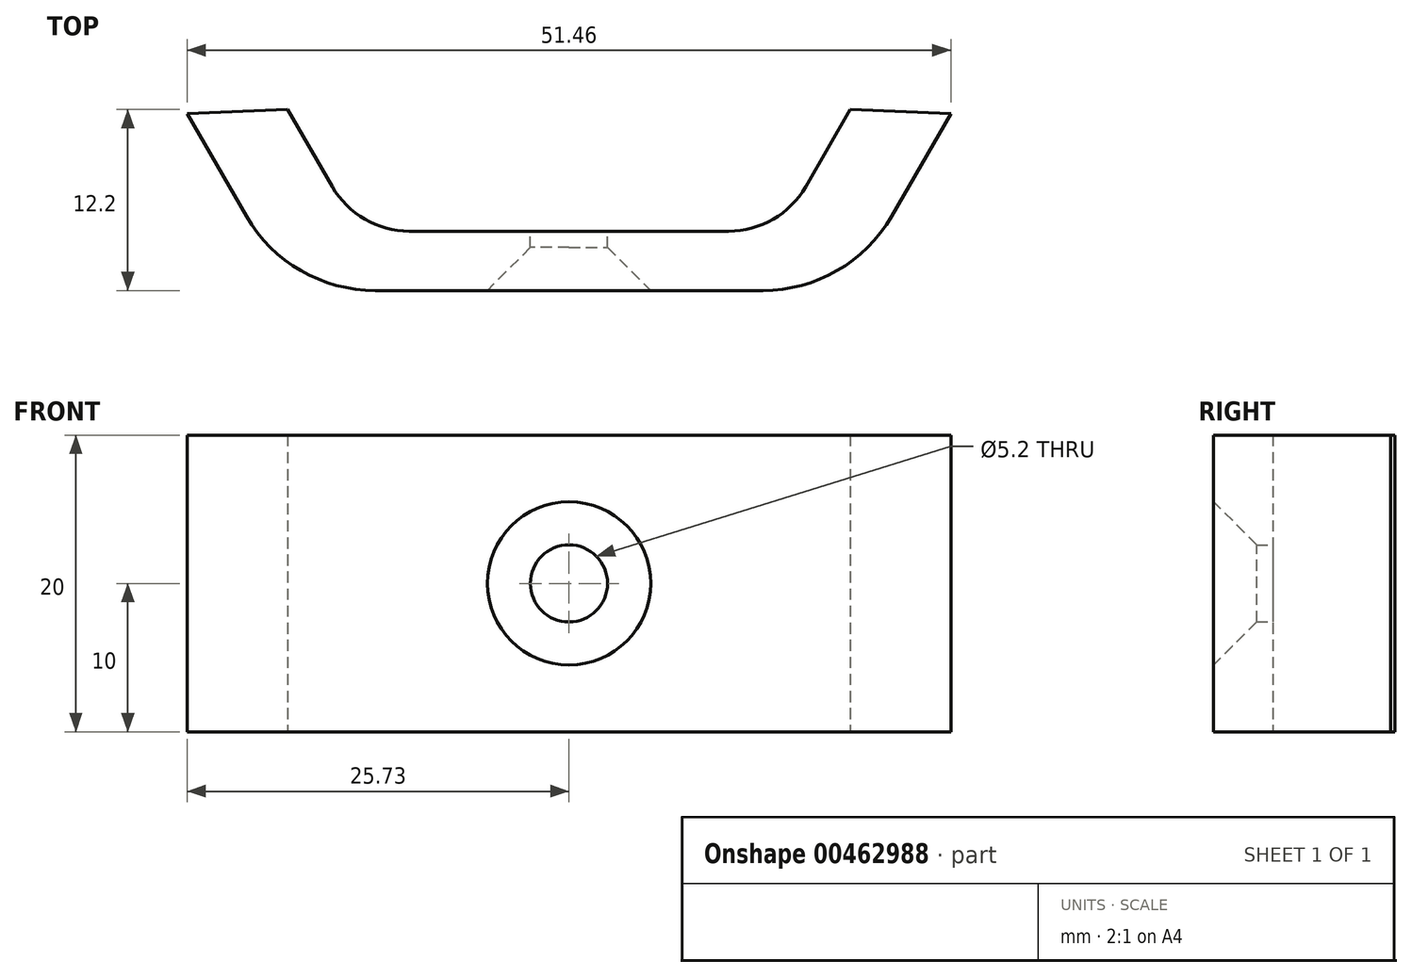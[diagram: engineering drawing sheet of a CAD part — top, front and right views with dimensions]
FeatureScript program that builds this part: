
annotation { "Feature Type Name" : "Feature", "Feature Type Description" : "" }
export const myFeature = defineFeature(function(context is Context, id is Id, definition is map)
    precondition{}
    {
        {
            var Q0;
            Q0=qCreatedBy(makeId("Top.planeOp"),FACE);
            var sketch = newSketch(context, id + "F0", { "sketchPlane" : qUnion([Q0])});
            skLineSegment(sketch, "E0", {"start": v(25.73, -37.83) * mm, "end": v(21.73, -44.76) * mm});
            skLineSegment(sketch, "E1", {"start": v(-25.73, -37.83) * mm, "end": v(-21.73, -44.76) * mm});
            skLineSegment(sketch, "E2", {"start": v(-13.07, -49.76) * mm, "end": v(13.07, -49.76) * mm});
            skPoint(sketch, "E3.visualSharp", {"position": v(-18.84, -49.76) * mm});
            skArc(sketch, "E3.filletArc", {"start": v(-21.73, -44.76) * mm, "mid": v(-18.07, -48.42) * mm, "end": v(-13.07, -49.76) * mm});
            skPoint(sketch, "E4.visualSharp", {"position": v(18.84, -49.76) * mm});
            skArc(sketch, "E4.filletArc", {"start": v(13.07, -49.76) * mm, "mid": v(18.07, -48.42) * mm, "end": v(21.73, -44.76) * mm});
            skLineSegment(sketch, "E5.bottom", {"start": v(10, -45.76) * mm, "end": v(-10, -45.76) * mm});
            skLineSegment(sketch, "E5.left", {"start": v(10, -45.76) * mm, "end": v(10, -3.76) * mm, "construction": true});
            skLineSegment(sketch, "E5.right", {"start": v(-10, -45.76) * mm, "end": v(-10, -3.76) * mm, "construction": true});
            skLineSegment(sketch, "E6", {"start": v(-29.83, -10.72) * mm, "end": v(-15.63, -35.33) * mm, "construction": true});
            skLineSegment(sketch, "E7", {"start": v(28.86, -12.4) * mm, "end": v(15.63, -35.33) * mm, "construction": true});
            skLineSegment(sketch, "E8", {"start": v(-20.45, -26.98) * mm, "end": v(-33.44, -34.48) * mm, "construction": true});
            skLineSegment(sketch, "E9", {"start": v(20.45, -26.98) * mm, "end": v(33.44, -34.48) * mm, "construction": true});
            skLineSegment(sketch, "E10", {"start": v(-36.16, -29.76) * mm, "end": v(-33.44, -34.48) * mm, "construction": true});
            skLineSegment(sketch, "E11", {"start": v(34.14, -33.27) * mm, "end": v(33.44, -34.48) * mm, "construction": true});
            skLineSegment(sketch, "E12", {"start": v(-11.83, -33.26) * mm, "end": v(12.94, -33.26) * mm, "construction": true});
            skLineSegment(sketch, "E13", {"start": v(-3.5, -45.32) * mm, "end": v(-3.5, -31.35) * mm, "construction": true});
            skLineSegment(sketch, "E14", {"start": v(3.5, -31.35) * mm, "end": v(3.5, -45.32) * mm, "construction": true});
            skLineSegment(sketch, "E15", {"start": v(-3.5, -31.35) * mm, "end": v(-32.45, -33.91) * mm, "construction": true});
            skLineSegment(sketch, "E16", {"start": v(-32.45, -33.91) * mm, "end": v(-32.01, -38.9) * mm, "construction": true});
            skLineSegment(sketch, "E17", {"start": v(-32.01, -38.9) * mm, "end": v(-3.5, -36.37) * mm, "construction": true});
            skLineSegment(sketch, "E18", {"start": v(3.5, -31.35) * mm, "end": v(32.5, -33.94) * mm, "construction": true});
            skLineSegment(sketch, "E19", {"start": v(32.5, -33.94) * mm, "end": v(32.06, -38.92) * mm, "construction": true});
            skLineSegment(sketch, "E20", {"start": v(32.06, -38.92) * mm, "end": v(3.5, -36.37) * mm, "construction": true});
            skLineSegment(sketch, "E21", {"start": v(-10, -45.76) * mm, "end": v(-10.76, -45.76) * mm});
            skLineSegment(sketch, "E22", {"start": v(-15.95, -42.76) * mm, "end": v(-18.95, -37.56) * mm});
            skLineSegment(sketch, "E23", {"start": v(-18.95, -37.56) * mm, "end": v(-25.73, -37.83) * mm});
            skLineSegment(sketch, "E24", {"start": v(10, -45.76) * mm, "end": v(10.76, -45.76) * mm});
            skLineSegment(sketch, "E25", {"start": v(15.95, -42.76) * mm, "end": v(18.95, -37.56) * mm});
            skLineSegment(sketch, "E26", {"start": v(18.95, -37.56) * mm, "end": v(25.73, -37.83) * mm});
            skPoint(sketch, "E27.visualSharp", {"position": v(-14.22, -45.76) * mm});
            skArc(sketch, "E27.filletArc", {"start": v(-15.95, -42.76) * mm, "mid": v(-13.76, -44.96) * mm, "end": v(-10.76, -45.76) * mm});
            skPoint(sketch, "E28.visualSharp", {"position": v(14.22, -45.76) * mm});
            skArc(sketch, "E28.filletArc", {"start": v(10.76, -45.76) * mm, "mid": v(13.76, -44.96) * mm, "end": v(15.95, -42.76) * mm});
            skPoint(sketch, "E29.orphan", {"position": v(-25.65, -47.96) * mm});
            skPoint(sketch, "E30.orphan", {"position": v(25.65, -47.96) * mm});
            skSolve(sketch);
        }
        {
            var Q0;
            Q0=qSketchRegion(id+"F0",true);
            extrude(context, id + "F1", {"entities" : qUnion([Q0]), "depth" : 20 * mm, "offsetDistance" : 25 * mm});
        }
        {
            var Q0;
            Q0=makeQuery(id+"F1.opExtrude","SWEPT_FACE",FACE,{"disambiguationData":[OSD([sQuery(id+"F0.wireOp",EDGE,"E2")])]});
            var sketch = newSketch(context, id + "F2", { "sketchPlane" : qUnion([Q0])});
            skCircle(sketch, "E31", {"center": v(0, 10) * mm, "radius": 5.5 * mm});
            skSolve(sketch);
        }
        {
            var Q0;
            Q0 = qSketchRegion(id + "F2", true);
            extrude(context, id + "F3", {"entities" : qUnion([Q0]), "operationType" : NewBodyOperationType.REMOVE, "oppositeDirection" : true, "depth" : 3.5 * mm, "offsetDistance" : 25 * mm, "hasDraft" : true, "draftAngle" : 45 * degree, "draftPullDirection" : true});
        }
        {
            var Q0;
            Q0=makeQuery(id+"F1.opExtrude","SWEPT_FACE",FACE,{"disambiguationData":[OSD([sQuery(id+"F0.wireOp",EDGE,"E5.bottom"),sQuery(id+"F0.wireOp",EDGE,"E21"),sQuery(id+"F0.wireOp",EDGE,"E24")])]});
            var sketch = newSketch(context, id + "F4", { "sketchPlane" : qUnion([Q0])});
            skCircle(sketch, "E32", {"center": v(0, 10) * mm, "radius": 2.6 * mm});
            skSolve(sketch);
        }
        {
            var Q0;
            Q0 = qSketchRegion(id + "F4", true);
            extrude(context, id + "F5", {"entities" : qUnion([Q0]), "operationType" : NewBodyOperationType.REMOVE, "oppositeDirection" : true, "depth" : 2 * mm, "offsetDistance" : 25 * mm});
        }
    });
